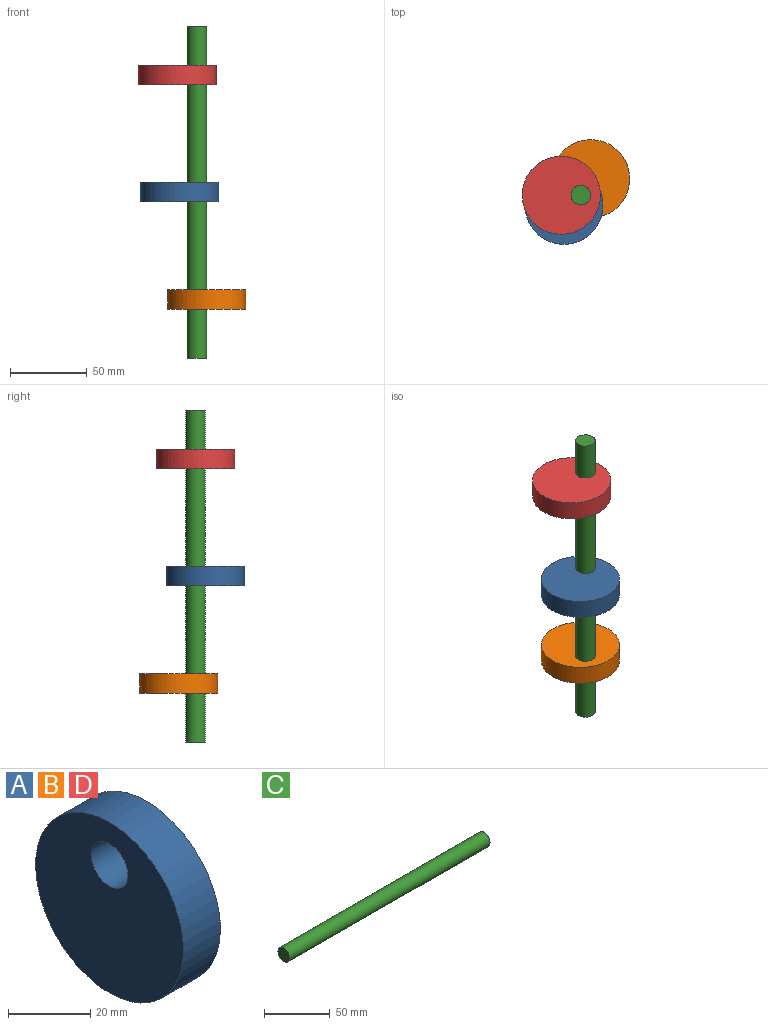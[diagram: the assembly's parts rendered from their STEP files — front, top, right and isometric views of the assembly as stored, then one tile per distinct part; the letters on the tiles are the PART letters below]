
ASSEMBLY  parts=4 mates=3
PART A: 4 faces, bbox 12.7x50.8x50.8 mm
  f0: plane 50.8x50.8mm, normal (1,0,0), area 1900.2mm2, adj f2,f3
  f1: plane 50.8x50.8mm, normal (-1,0,0), area 1900.2mm2, adj f2,f3
  f2: cylinder r=25.4mm len=50.8mm, axis (-1,0,0), area 2026.8mm2, adj f0,f1
  f3: cylinder r=6.35mm len=12.7mm, axis (-1,0,0), area 506.7mm2, adj f0,f1
PART B: same geometry as A
PART C: 3 faces, bbox 215.9x12.7x12.7 mm
  f0: plane 12.7x12.7mm, normal (-1,0,0), area 126.7mm2, adj f2
  f1: plane 12.7x12.7mm, normal (1,0,0), area 126.7mm2, adj f2
  f2: cylinder r=6.35mm len=215.9mm, axis (-1,0,0), area 8614mm2, adj f0,f1
PART D: same geometry as A
PLACE A rot(axis=(-0.25,0.94,0.25),93.8deg) t=(-49.49,-28.57,-177.8)mm
PLACE B rot(axis=(0.65,0.38,-0.65),138.6deg) t=(28.58,49.49,-247.65)mm
PLACE C rot(axis=(0,1,0),90deg) t=(-57.15,0,-101.6)mm
PLACE D rot(axis=(0,1,0),90deg) t=(-57.15,0,-101.6)mm
MATE fastened C.f2 <-> D.f3  axis (0,0,1) through (0,0,-31.75)mm
MATE fastened C.f2 <-> B.f3  axis (0,0,1) through (0,0,-171.45)mm
MATE fastened C.f2 <-> A.f3  axis (0,0,1) through (0,0,-101.6)mm
